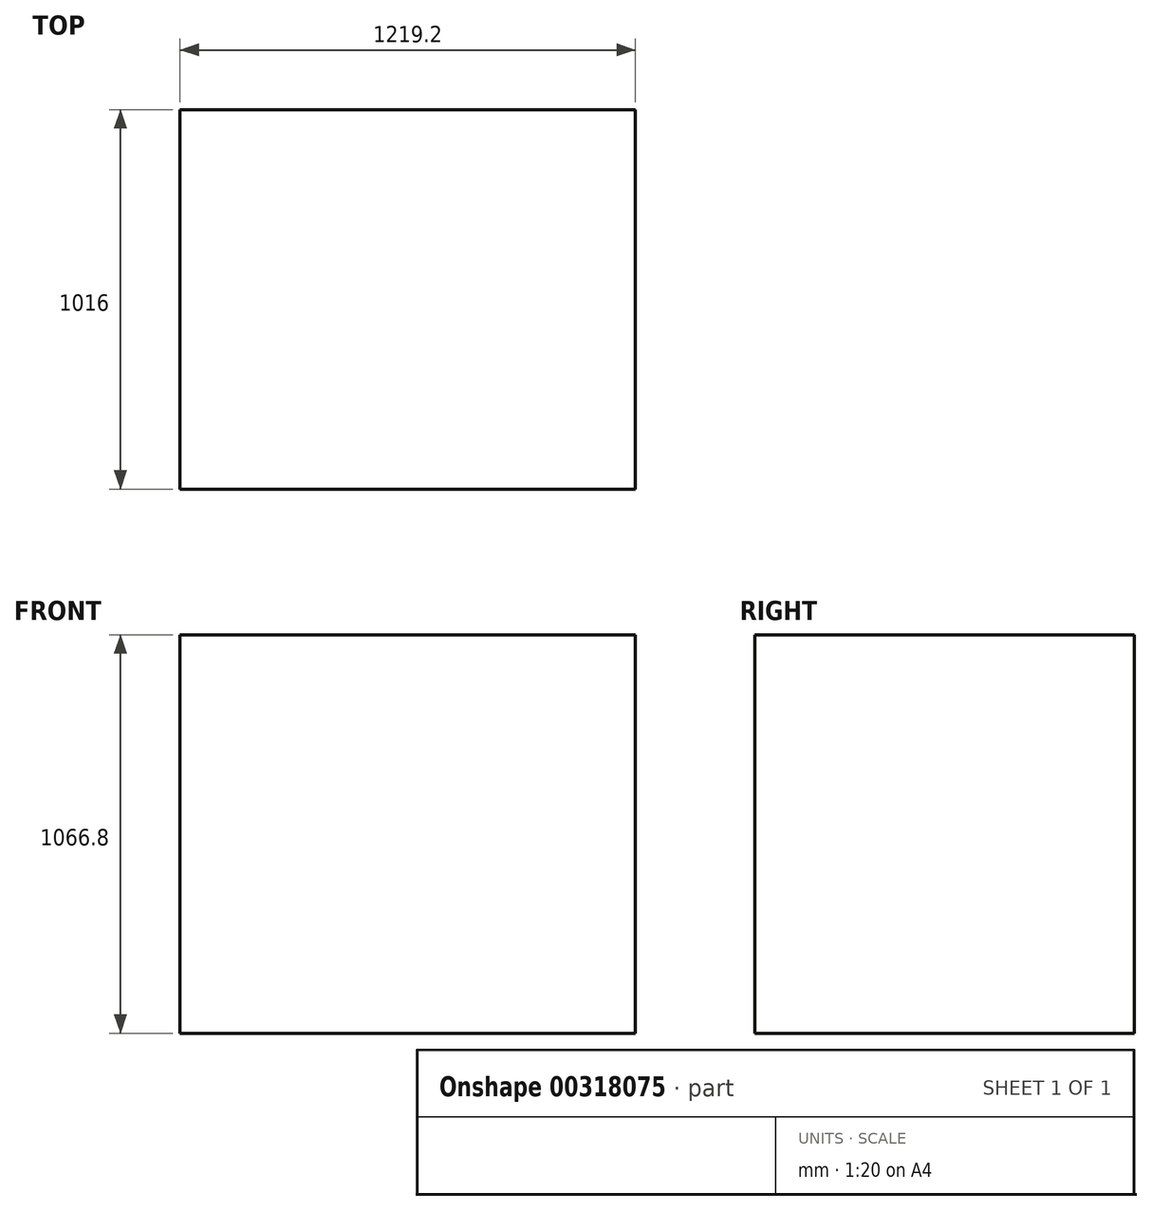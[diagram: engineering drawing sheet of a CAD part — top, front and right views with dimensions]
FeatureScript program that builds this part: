
annotation { "Feature Type Name" : "Feature", "Feature Type Description" : "" }
export const myFeature = defineFeature(function(context is Context, id is Id, definition is map)
    precondition{}
    {
        {
            var Q0;
            Q0=qCreatedBy(makeId("Front.planeOp"),FACE);
            var sketch = newSketch(context, id + "F0", { "sketchPlane" : qUnion([Q0])});
            skLineSegment(sketch, "E0.bottom", {"start": v(-1219.2, 1066.8) * mm, "end": v(0, 1066.8) * mm});
            skLineSegment(sketch, "E0.top", {"start": v(-1219.2, 0) * mm, "end": v(0, 0) * mm});
            skLineSegment(sketch, "E0.left", {"start": v(-1219.2, 1066.8) * mm, "end": v(-1219.2, 0) * mm});
            skLineSegment(sketch, "E0.right", {"start": v(0, 1066.8) * mm, "end": v(0, 0) * mm});
            skSolve(sketch);
        }
        {
            var Q0;
            Q0=qSketchRegion(id+"F0",true);
            extrude(context, id + "F1", {"entities" : qUnion([Q0]), "depth" : 1016 * mm, "offsetDistance" : 25.4 * mm});
        }
    });
